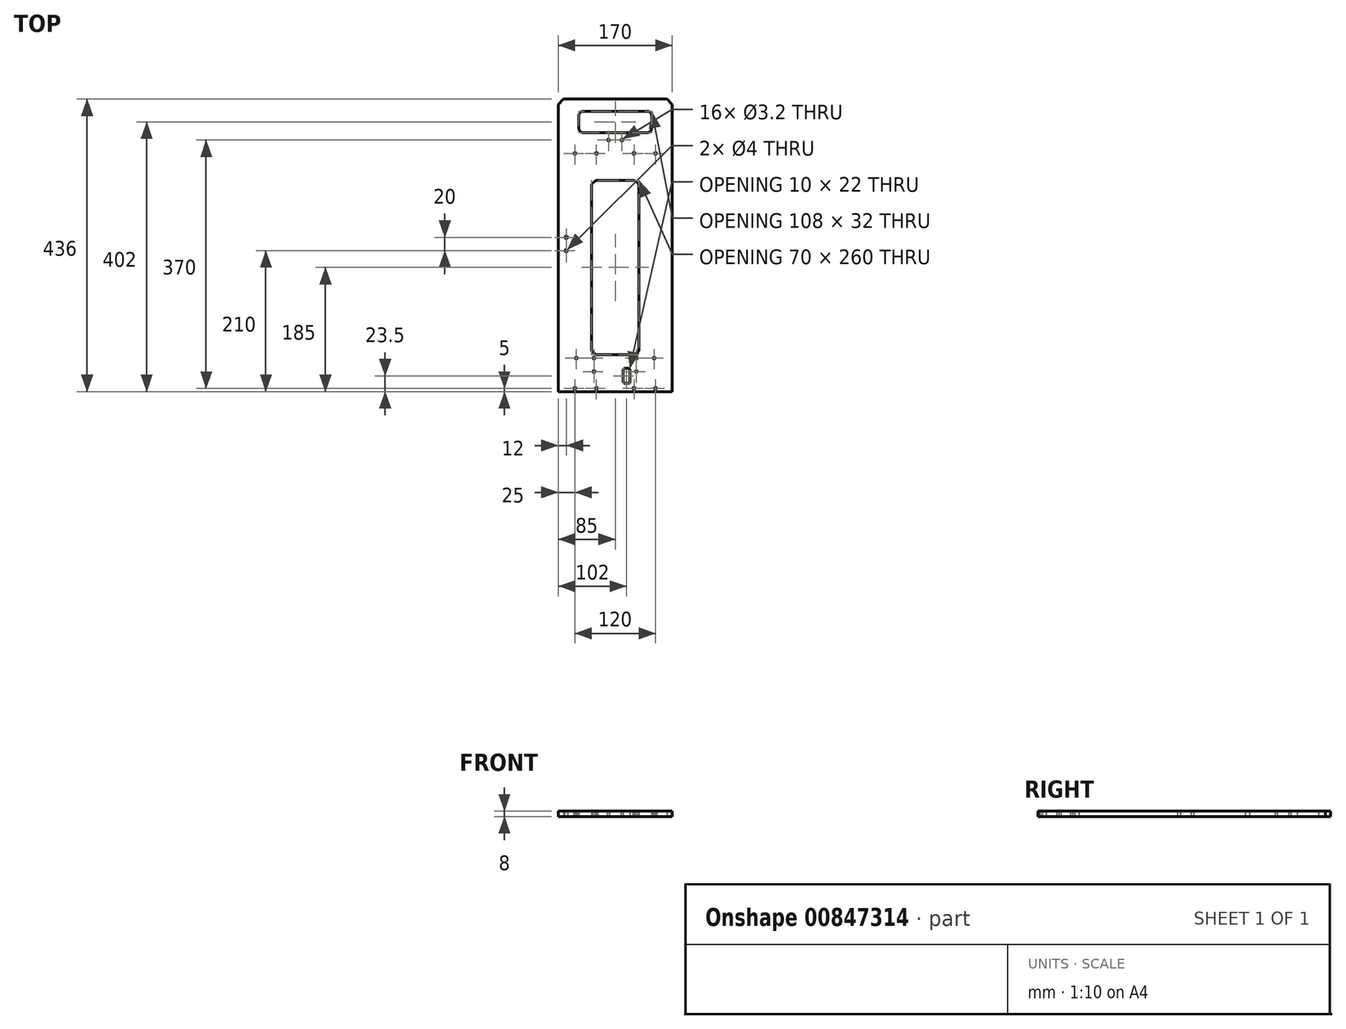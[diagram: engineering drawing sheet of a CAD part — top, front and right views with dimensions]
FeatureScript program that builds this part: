
annotation { "Feature Type Name" : "Feature", "Feature Type Description" : "" }
export const myFeature = defineFeature(function(context is Context, id is Id, definition is map)
    precondition{}
    {
        {
            var Q0;
            Q0=qCreatedBy(makeId("Top.planeOp"),FACE);
            var sketch = newSketch(context, id + "F0", { "sketchPlane" : qUnion([Q0])});
            skLineSegment(sketch, "E0", {"start": v(85, 210) * mm, "end": v(85, -218) * mm});
            skLineSegment(sketch, "E1", {"start": v(85, 210) * mm, "end": v(77, 218) * mm});
            skLineSegment(sketch, "E2", {"start": v(85, -218) * mm, "end": v(-85, -218) * mm});
            skLineSegment(sketch, "E3", {"start": v(-77, 218) * mm, "end": v(77, 218) * mm});
            skLineSegment(sketch, "E4", {"start": v(-85, -218) * mm, "end": v(-85, 210) * mm});
            skLineSegment(sketch, "E5", {"start": v(-85, 210) * mm, "end": v(-77, 218) * mm});
            skCircle(sketch, "E6", {"center": v(-31.5, -168) * mm, "radius": 1.6 * mm});
            skCircle(sketch, "E7", {"center": v(-31.5, -188) * mm, "radius": 1.6 * mm});
            skCircle(sketch, "E8", {"center": v(31.5, -188) * mm, "radius": 1.6 * mm});
            skCircle(sketch, "E9", {"center": v(31.5, -168) * mm, "radius": 1.6 * mm});
            skArc(sketch, "E10", {"start": v(14, -183.5) * mm, "mid": v(12.59, -184.09) * mm, "end": v(12, -185.5) * mm});
            skLineSegment(sketch, "E11", {"start": v(14, -183.5) * mm, "end": v(20, -183.5) * mm});
            skLineSegment(sketch, "E12", {"start": v(12, -203.5) * mm, "end": v(12, -185.5) * mm});
            skArc(sketch, "E13", {"start": v(22, -185.5) * mm, "mid": v(21.41, -184.09) * mm, "end": v(20, -183.5) * mm});
            skArc(sketch, "E14", {"start": v(12, -203.5) * mm, "mid": v(12.59, -204.91) * mm, "end": v(14, -205.5) * mm});
            skLineSegment(sketch, "E15", {"start": v(22, -185.5) * mm, "end": v(22, -203.5) * mm});
            skLineSegment(sketch, "E16", {"start": v(20, -205.5) * mm, "end": v(14, -205.5) * mm});
            skArc(sketch, "E17", {"start": v(20, -205.5) * mm, "mid": v(21.41, -204.91) * mm, "end": v(22, -203.5) * mm});
            skCircle(sketch, "E18", {"center": v(-58, -168) * mm, "radius": 1.6 * mm});
            skCircle(sketch, "E19", {"center": v(-73, -8) * mm, "radius": 2 * mm});
            skCircle(sketch, "E20", {"center": v(-73, 12) * mm, "radius": 2 * mm});
            skLineSegment(sketch, "E21", {"start": v(-29, 97) * mm, "end": v(29, 97) * mm});
            skLineSegment(sketch, "E22", {"start": v(-29, 97) * mm, "end": v(-35, 91) * mm});
            skLineSegment(sketch, "E23", {"start": v(29, 97) * mm, "end": v(35, 91) * mm});
            skLineSegment(sketch, "E24", {"start": v(-35, -157) * mm, "end": v(-35, 91) * mm});
            skLineSegment(sketch, "E25", {"start": v(35, 91) * mm, "end": v(35, -157) * mm});
            skLineSegment(sketch, "E26", {"start": v(-29, -163) * mm, "end": v(-35, -157) * mm});
            skLineSegment(sketch, "E27", {"start": v(35, -157) * mm, "end": v(29, -163) * mm});
            skLineSegment(sketch, "E28", {"start": v(29, -163) * mm, "end": v(-29, -163) * mm});
            skCircle(sketch, "E29", {"center": v(60, 137) * mm, "radius": 1.6 * mm});
            skCircle(sketch, "E30", {"center": v(58, -168) * mm, "radius": 1.6 * mm});
            skCircle(sketch, "E31", {"center": v(-60, 137) * mm, "radius": 1.6 * mm});
            skCircle(sketch, "E32", {"center": v(-28, 137) * mm, "radius": 1.6 * mm});
            skCircle(sketch, "E33", {"center": v(28, 137) * mm, "radius": 1.6 * mm});
            skCircle(sketch, "E34", {"center": v(60, -213) * mm, "radius": 1.6 * mm});
            skCircle(sketch, "E35", {"center": v(28, -213) * mm, "radius": 1.6 * mm});
            skCircle(sketch, "E36", {"center": v(-28, -213) * mm, "radius": 1.6 * mm});
            skCircle(sketch, "E37", {"center": v(-60, -213) * mm, "radius": 1.6 * mm});
            skCircle(sketch, "E38", {"center": v(10, 157) * mm, "radius": 1.6 * mm});
            skCircle(sketch, "E39", {"center": v(-10, 157) * mm, "radius": 1.6 * mm});
            skArc(sketch, "E40", {"start": v(-48, 200) * mm, "mid": v(-52.24, 198.24) * mm, "end": v(-54, 194) * mm});
            skLineSegment(sketch, "E41", {"start": v(-54, 174) * mm, "end": v(-54, 194) * mm});
            skArc(sketch, "E42", {"start": v(-54, 174) * mm, "mid": v(-52.24, 169.76) * mm, "end": v(-48, 168) * mm});
            skLineSegment(sketch, "E43", {"start": v(48, 168) * mm, "end": v(-48, 168) * mm});
            skArc(sketch, "E44", {"start": v(48, 168) * mm, "mid": v(52.24, 169.76) * mm, "end": v(54, 174) * mm});
            skLineSegment(sketch, "E45", {"start": v(54, 194) * mm, "end": v(54, 174) * mm});
            skArc(sketch, "E46", {"start": v(54, 194) * mm, "mid": v(52.24, 198.24) * mm, "end": v(48, 200) * mm});
            skLineSegment(sketch, "E47", {"start": v(-48, 200) * mm, "end": v(48, 200) * mm});
            skSolve(sketch);
        }
        {
            var Q0;
            Q0=qSketchRegion(id+"F0",true);
            extrude(context, id + "F1", {"entities" : qUnion([Q0]), "depth" : 8 * mm});
        }
    });
